# Revit family: revitupgrade
name_source: partatom
category: Furniture
units: mm (PartAtom-declared; Revit-internal decimal feet)

## family parameters
Always vertical = Yes
Cut with Voids When Loaded = No
Enable Cutting in Views = No
OmniClass Number = 23.40.70.14.64.11
OmniClass Title = Office Furniture
Render Appearance Source = Family Geometry
Room Calculation Point = No
Shared = No
Work Plane-Based = No

## types (4) — shared parameters
Assembly Code = E2020200
Base = Steelcase_Plastic_6249_PlatinumSolid/Nickel
Caster/Bracket = Steelcase - 0835 Black
Default Elevation = 0.00"
Description = The Node chair is mobile and supports all the ways students learn. It’s designed for quick, easy transitions in the classroom, and to support learning modes across the campus.
Manufacturer = Steelcase
Release Date = November 2022
Tablet = Steelcase - 6249 Platinum Solid
URL = https://www.steelcase.com

## per-type parameters (varying)
| type | Cup Holder | Style Number(s) | Tablet Stand | Worksurface |
| Personal Worksurface/Tablet Stand | No | 480E150 | Yes | Yes |
| Personal Worksurface/Cup Holder/Tablet Stand | Yes | 480E150 | Yes | Yes |
| Personal Worksurface | No | 480E150 | No | Yes |
| Without Personal Worksurface | No | 480E130 | No | No |

## geometry (parser evidence)
native form markers: Sweep x3
no freeform markers — native parametric forms only
